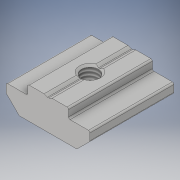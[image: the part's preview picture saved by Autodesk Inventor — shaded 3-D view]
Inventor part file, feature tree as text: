
AUTODESK INVENTOR PART (.ipt)
format: ipt  version: 2019 (Build 230136000, 136)  size: 155,648 bytes
history: native  units: mm
features: sketch x2, extrude x1, revolve x1, thread x1
ambient origin geometry x8: Origin, YZ Plane, XZ Plane, XY Plane, X Axis, Y Axis, Z Axis, Center Point
bodies: Solid1 (feature_tree)
feature tree (5):
  extrude  "Extrusion1"  TaperAngle=360.0deg  [1 undecoded]
  revolve  "Revolution1"  [1 undecoded]
  thread  "Thread1"  [1 undecoded]
  sketch  "Sketch_1"  dims[d0=16.0mm d1=0.0mm d2=360.0deg]
  sketch  "Sketch_2"  dims[d3=5.242mm d4=0.0mm]
note: 3 required parameter values undecoded (feature->parameter linkage not recoverable at this tier; creation-order binding heuristic only, values carry confidence <= 0.55)
